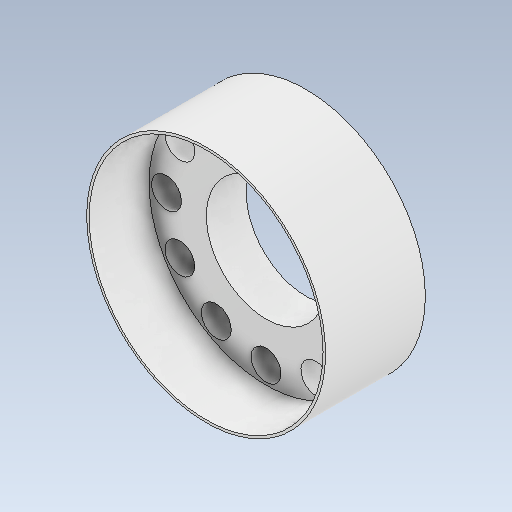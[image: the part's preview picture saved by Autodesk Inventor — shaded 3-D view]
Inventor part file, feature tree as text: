
AUTODESK INVENTOR PART (.ipt)
format: ipt  version: 2023 (Build 270158000, 158)  size: 180,224 bytes
history: native  units: in
note: dims shown in document units (in); Inventor stores cm internally (conversion verified against a paired STEP export)
features: extrude x3, sketch x1, pattern_circular x1
ambient origin geometry x8: Origin, YZ Plane, XZ Plane, XY Plane, X Axis, Y Axis, Z Axis, Center Point
bodies: Solid1 (feature_tree)
feature tree (5):
  sketch  "Sketch1"  dims[d0=3.0in d1=0.0315in d2=1.253in d3=0.0in d4=1.5in d5=0.5in d6=0.0in d7=2.5in d8=0.375in d9=0.5in d10=0.0in d11=4.7244in d12=360.0deg]
  extrude  "Extrusion1"  Depth=0.5in
  extrude  "Extrusion2"  Depth=1.253in TaperAngle=0.0deg
  extrude  "Extrusion3"  Depth=1.5in
  pattern_circular  "Circular Pattern1"  [2 undecoded]
note: 2 required parameter values undecoded (feature->parameter linkage not recoverable at this tier; creation-order binding heuristic only, values carry confidence <= 0.55)
